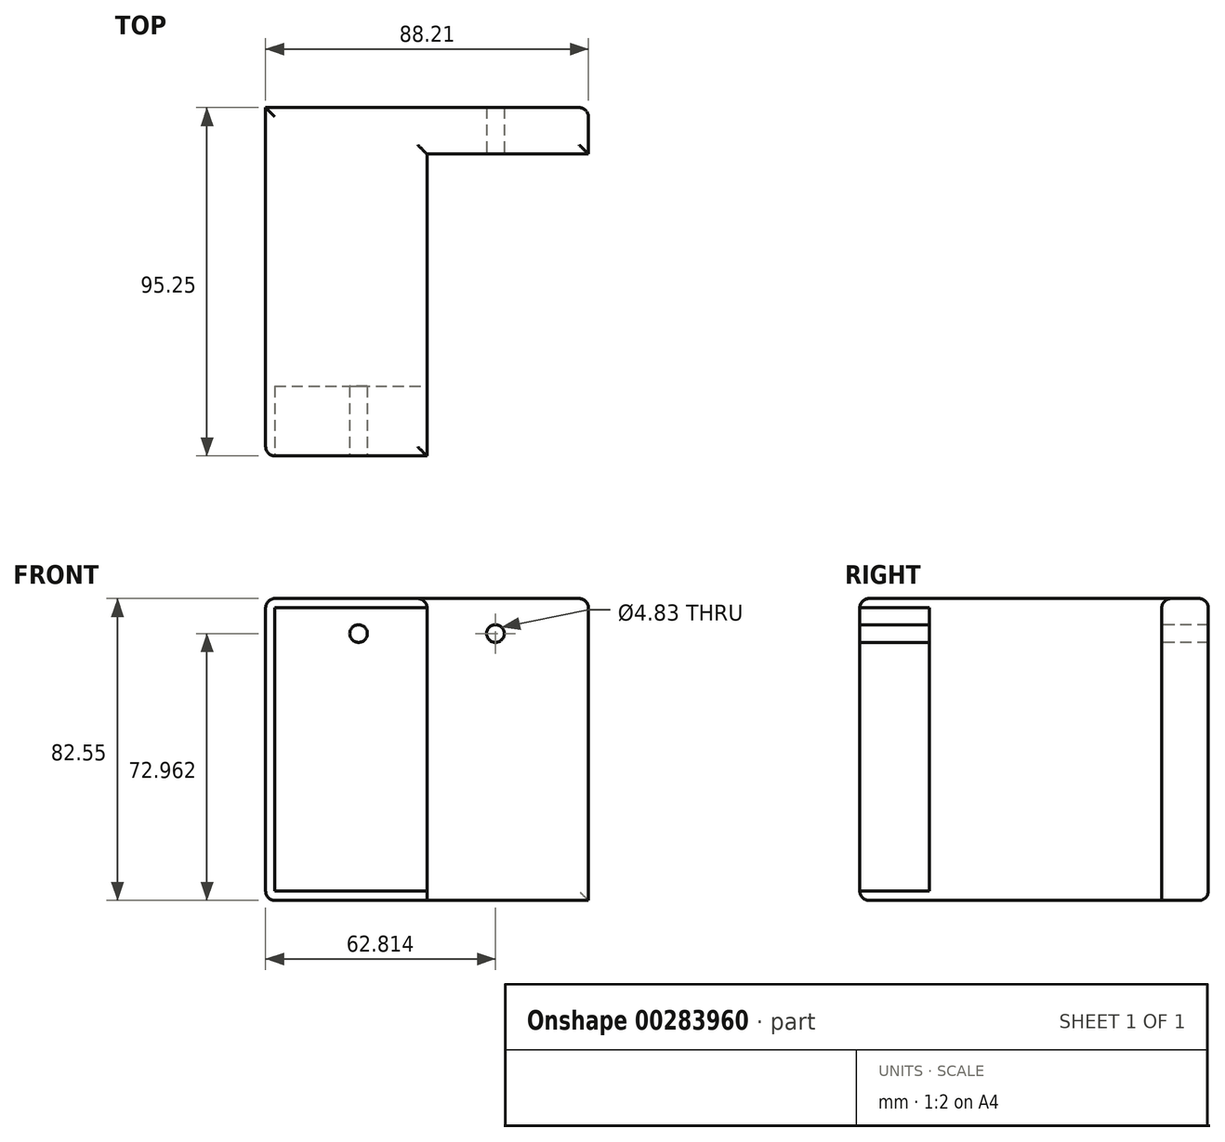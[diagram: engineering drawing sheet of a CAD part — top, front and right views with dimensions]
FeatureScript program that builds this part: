
annotation { "Feature Type Name" : "Feature", "Feature Type Description" : "" }
export const myFeature = defineFeature(function(context is Context, id is Id, definition is map)
    precondition{}
    {
        {
            var Q0;
            Q0=qCreatedBy(makeId("Front.planeOp"),FACE);
            var sketch = newSketch(context, id + "F0", { "sketchPlane" : qUnion([Q0])});
            skLineSegment(sketch, "E0", {"start": v(0, 0) * mm, "end": v(88.21, 0) * mm});
            skLineSegment(sketch, "E1.0", {"start": v(0, 82.55) * mm, "end": v(88.21, 82.55) * mm});
            skLineSegment(sketch, "E2", {"start": v(0, 0) * mm, "end": v(0, 82.55) * mm});
            skLineSegment(sketch, "E3", {"start": v(88.21, 0) * mm, "end": v(88.21, 82.55) * mm});
            skSolve(sketch);
        }
        {
            var Q0;
            Q0 = qSketchRegion(id + "F0", true);
            extrude(context, id + "F1", {"entities" : qUnion([Q0]), "depth" : 95.25 * mm});
        }
        {
            var Q0;
            Q0=makeQuery(id+"F1.opExtrude","CAP_FACE",FACE,{"disambiguationData":[OSD([sQuery(id+"F0.wireOp",EDGE,"E0"),sQuery(id+"F0.wireOp",EDGE,"E1.0"),sQuery(id+"F0.wireOp",EDGE,"E2"),sQuery(id+"F0.wireOp",EDGE,"E3")])],"isStart":false});
            var sketch = newSketch(context, id + "F2", { "sketchPlane" : qUnion([Q0])});
            skLineSegment(sketch, "E4.bottom", {"start": v(88.21, 0) * mm, "end": v(44.1, 0) * mm});
            skLineSegment(sketch, "E4.top", {"start": v(88.21, 82.55) * mm, "end": v(44.1, 82.55) * mm});
            skLineSegment(sketch, "E4.left", {"start": v(88.21, 0) * mm, "end": v(88.21, 82.55) * mm});
            skLineSegment(sketch, "E4.right", {"start": v(44.1, 0) * mm, "end": v(44.1, 82.55) * mm});
            skSolve(sketch);
        }
        {
            var Q0;
            Q0=makeQuery(id+"F2.imprint","IMPRINT",FACE,{"disambiguationData":[TD([[makeQuery(id+"F2.imprint","IMPRINT",EDGE,{"derivedFrom":sQuery(id+"F2.wireOp",EDGE,"E4.bottom")}),1.0]])]});
            extrude(context, id + "F3", {"entities" : qUnion([Q0]), "operationType" : NewBodyOperationType.REMOVE, "oppositeDirection" : true, "depth" : 82.55 * mm});
        }
        {
            var Q0;
            Q0=makeQuery(id+"F3.boolean.opBoolean","COPY",EDGE,{"derivedFrom":makeQuery(id+"F3.opExtrude","CAP_EDGE",EDGE,{"disambiguationData":[OSD([sQuery(id+"F2.wireOp",EDGE,"E4.right")])],"isStart":true})});
            var Q1;
            Q1=makeQuery(id+"F1.opExtrude","CAP_EDGE",EDGE,{"disambiguationData":[OSD([sQuery(id+"F0.wireOp",EDGE,"E3")])],"isStart":true});
            var Q2;
            Q2=makeQuery(id+"F3.boolean.opBoolean","COPY",EDGE,{"derivedFrom":makeQuery(id+"F3.opExtrude","CAP_EDGE",EDGE,{"disambiguationData":[OSD([sQuery(id+"F2.wireOp",EDGE,"E4.left")])],"isStart":false})});
            var Q3;
            Q3=makeQuery(id+"F1.opExtrude","SWEPT_EDGE",EDGE,{"disambiguationData":[OSD([sQuery(id+"F0.wireOp",EDGE,"E0"),sQuery(id+"F0.wireOp",EDGE,"E2")])]});
            var Q4;
            Q4=makeQuery(id+"F1.opExtrude","CAP_EDGE",EDGE,{"disambiguationData":[OSD([sQuery(id+"F0.wireOp",EDGE,"E0")])],"isStart":false});
            var Q5;
            Q5=makeQuery(id+"F1.opExtrude","CAP_EDGE",EDGE,{"disambiguationData":[OSD([sQuery(id+"F0.wireOp",EDGE,"E2")])],"isStart":false});
            var Q6;
            Q6=makeQuery(id+"F1.opExtrude","CAP_EDGE",EDGE,{"disambiguationData":[OSD([sQuery(id+"F0.wireOp",EDGE,"E1.0")])],"isStart":false});
            var Q7;
            Q7=makeQuery(id+"F1.opExtrude","SWEPT_EDGE",EDGE,{"disambiguationData":[OSD([sQuery(id+"F0.wireOp",EDGE,"E1.0"),sQuery(id+"F0.wireOp",EDGE,"E2")])]});
            var Q8;
            Q8=makeQuery(id+"F1.opExtrude","SWEPT_FACE",FACE,{"disambiguationData":[OSD([sQuery(id+"F0.wireOp",EDGE,"E1.0")])]});
            var Q9;
            Q9=makeQuery(id+"F3.boolean.opBoolean","COPY",EDGE,{"derivedFrom":makeQuery(id+"F3.opExtrude","SWEPT_EDGE",EDGE,{"disambiguationData":[OSD([sQuery(id+"F0.wireOp",EDGE,"E0"),sQuery(id+"F2.wireOp",EDGE,"E4.bottom"),sQuery(id+"F2.wireOp",EDGE,"E4.right")])]})});
            var Q10;
            Q10=makeQuery(id+"F3.boolean.opBoolean","COPY",EDGE,{"derivedFrom":makeQuery(id+"F3.opExtrude","CAP_EDGE",EDGE,{"disambiguationData":[OSD([sQuery(id+"F2.wireOp",EDGE,"E4.bottom")])],"isStart":false})});
            var Q11;
            Q11=makeQuery(id+"F1.opExtrude","CAP_EDGE",EDGE,{"disambiguationData":[OSD([sQuery(id+"F0.wireOp",EDGE,"E0")])],"isStart":true});
            fillet(context, id + "F4", {"entities" : qUnion([Q0, Q1, Q2, Q3, Q4, Q5, Q6, Q7, Q8, Q9, Q10, Q11]), "radius" : 2.54 * mm, "tangentPropagation" : true, "allowEdgeOverflow" : false});
        }
        {
            var Q0;
            Q0=makeQuery(id+"F1.opExtrude","CAP_FACE",FACE,{"disambiguationData":[OSD([sQuery(id+"F0.wireOp",EDGE,"E0"),sQuery(id+"F0.wireOp",EDGE,"E1.0"),sQuery(id+"F0.wireOp",EDGE,"E2"),sQuery(id+"F0.wireOp",EDGE,"E3")])],"isStart":false});
            var sketch = newSketch(context, id + "F5", { "sketchPlane" : qUnion([Q0])});
            skLineSegment(sketch, "E5", {"start": v(0, 0) * mm, "end": v(44.1, 0) * mm});
            skLineSegment(sketch, "E6.0", {"start": v(0, 6.29) * mm, "end": v(25.4, 6.29) * mm});
            skCircle(sketch, "E7", {"center": v(25.4, 6.29) * mm, "radius": 2.41 * mm});
            skCircle(sketch, "E8.MirrorC", {"center": v(25.4, 72.96) * mm, "radius": 2.41 * mm});
            skLineSegment(sketch, "E9", {"start": v(0, 0) * mm, "end": v(50.06, 0) * mm});
            skLineSegment(sketch, "E10", {"start": v(44.1, 0) * mm, "end": v(44.1, 30.36) * mm});
            skCircle(sketch, "E11.MirrorC", {"center": v(62.81, 6.29) * mm, "radius": 2.41 * mm});
            skCircle(sketch, "E12.MirrorC", {"center": v(62.81, 72.96) * mm, "radius": 2.41 * mm});
            skSolve(sketch);
        }
        {
            var Q0;
            Q0=makeQuery(id+"F5.imprint","IMPRINT",FACE,{"disambiguationData":[TD([[makeQuery(id+"F5.imprint","IMPRINT",EDGE,{"derivedFrom":sQuery(id+"F5.wireOp",EDGE,"E7")}),1.0]])]});
            var Q1;
            Q1=makeQuery(id+"F5.imprint","IMPRINT",FACE,{"disambiguationData":[TD([[makeQuery(id+"F5.imprint","IMPRINT",EDGE,{"derivedFrom":sQuery(id+"F5.wireOp",EDGE,"E8.MirrorC")}),-1.0]])]});
            extrude(context, id + "F6", {"entities" : qUnion([Q0, Q1]), "operationType" : NewBodyOperationType.REMOVE, "oppositeDirection" : true, "depth" : 19.05 * mm});
        }
        {
            var Q0;
            Q0=makeQuery(id+"F5.imprint","IMPRINT",FACE,{"disambiguationData":[TD([[makeQuery(id+"F5.imprint","IMPRINT",EDGE,{"derivedFrom":sQuery(id+"F5.wireOp",EDGE,"E11.MirrorC")}),-1.0]])]});
            var Q1;
            Q1=makeQuery(id+"F5.imprint","IMPRINT",FACE,{"disambiguationData":[TD([[makeQuery(id+"F5.imprint","IMPRINT",EDGE,{"derivedFrom":sQuery(id+"F5.wireOp",EDGE,"E12.MirrorC")}),1.0]])]});
            extrude(context, id + "F7", {"entities" : qUnion([Q0, Q1]), "operationType" : NewBodyOperationType.REMOVE, "oppositeDirection" : true, "depth" : 127 * mm});
        }
    });
